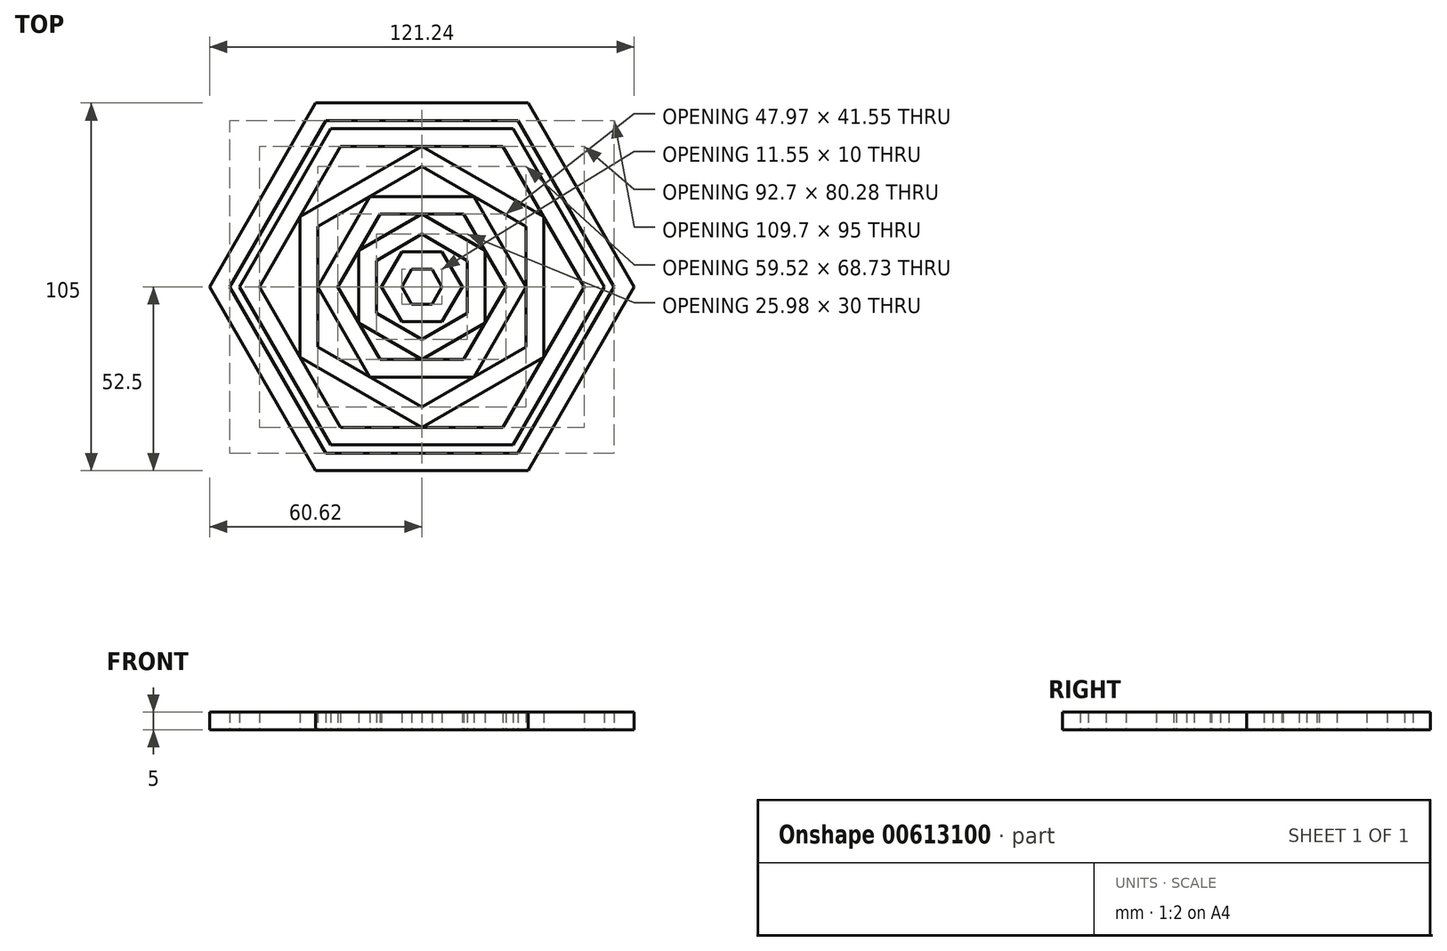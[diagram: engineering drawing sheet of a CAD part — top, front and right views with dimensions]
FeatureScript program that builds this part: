
annotation { "Feature Type Name" : "Feature", "Feature Type Description" : "" }
export const myFeature = defineFeature(function(context is Context, id is Id, definition is map)
    precondition{}
    {
        {
            var Q0;
            Q0=qCreatedBy(makeId("Top.planeOp"),FACE);
            var sketch = newSketch(context, id + "F0", { "sketchPlane" : qUnion([Q0])});
            skCircle(sketch, "E0.cCircle", {"center": v(0, 0) * mm, "radius": 47.5 * mm, "construction": true});
            skLineSegment(sketch, "E0.0", {"start": v(-27.42, 47.5) * mm, "end": v(27.42, 47.5) * mm});
            skLineSegment(sketch, "E0.1", {"start": v(27.42, 47.5) * mm, "end": v(54.85, 0) * mm});
            skLineSegment(sketch, "E0.2", {"start": v(54.85, 0) * mm, "end": v(27.42, -47.5) * mm});
            skLineSegment(sketch, "E0.3", {"start": v(27.42, -47.5) * mm, "end": v(-27.42, -47.5) * mm});
            skLineSegment(sketch, "E0.4", {"start": v(-27.42, -47.5) * mm, "end": v(-54.85, 0) * mm});
            skLineSegment(sketch, "E0.5", {"start": v(-54.85, 0) * mm, "end": v(-27.42, 47.5) * mm});
            skPoint(sketch, "E0.0.midPoint", {"position": v(0, 47.5) * mm});
            skLineSegment(sketch, "E1.0", {"start": v(-60.62, 0) * mm, "end": v(-30.31, 52.5) * mm});
            skLineSegment(sketch, "E1.1", {"start": v(30.31, 52.5) * mm, "end": v(60.62, 0) * mm});
            skLineSegment(sketch, "E1.2", {"start": v(60.62, 0) * mm, "end": v(30.31, -52.5) * mm});
            skLineSegment(sketch, "E1.3", {"start": v(-30.31, 52.5) * mm, "end": v(30.31, 52.5) * mm});
            skLineSegment(sketch, "E1.4", {"start": v(30.31, -52.5) * mm, "end": v(-30.31, -52.5) * mm});
            skLineSegment(sketch, "E1.5", {"start": v(-30.31, -52.5) * mm, "end": v(-60.62, 0) * mm});
            skCircle(sketch, "E2.cCircle", {"center": v(0, 0) * mm, "radius": 5 * mm, "construction": true});
            skLineSegment(sketch, "E2.0", {"start": v(-2.89, 5) * mm, "end": v(2.89, 5) * mm});
            skLineSegment(sketch, "E2.1", {"start": v(2.89, 5) * mm, "end": v(5.77, 0) * mm});
            skLineSegment(sketch, "E2.2", {"start": v(5.77, 0) * mm, "end": v(2.89, -5) * mm});
            skLineSegment(sketch, "E2.3", {"start": v(2.89, -5) * mm, "end": v(-2.89, -5) * mm});
            skLineSegment(sketch, "E2.4", {"start": v(-2.89, -5) * mm, "end": v(-5.77, 0) * mm});
            skLineSegment(sketch, "E2.5", {"start": v(-5.77, 0) * mm, "end": v(-2.89, 5) * mm});
            skPoint(sketch, "E2.0.midPoint", {"position": v(0, 5) * mm});
            skLineSegment(sketch, "E3.0", {"start": v(-11.55, 0) * mm, "end": v(-5.77, 10) * mm});
            skLineSegment(sketch, "E3.1", {"start": v(5.77, 10) * mm, "end": v(11.55, 0) * mm});
            skLineSegment(sketch, "E3.2", {"start": v(11.55, 0) * mm, "end": v(5.77, -10) * mm});
            skLineSegment(sketch, "E3.3", {"start": v(-5.77, 10) * mm, "end": v(5.77, 10) * mm});
            skLineSegment(sketch, "E3.4", {"start": v(5.77, -10) * mm, "end": v(-5.77, -10) * mm});
            skLineSegment(sketch, "E3.5", {"start": v(-5.77, -10) * mm, "end": v(-11.55, 0) * mm});
            skCircle(sketch, "E4.cCircle", {"center": v(0, 0) * mm, "radius": 13 * mm, "construction": true});
            skLineSegment(sketch, "E4.0", {"start": v(13, 7.5) * mm, "end": v(13, -7.5) * mm});
            skLineSegment(sketch, "E4.1", {"start": v(13, -7.5) * mm, "end": v(0, -15) * mm});
            skLineSegment(sketch, "E4.2", {"start": v(0, -15) * mm, "end": v(-13, -7.5) * mm});
            skLineSegment(sketch, "E4.3", {"start": v(-13, -7.5) * mm, "end": v(-13, 7.5) * mm});
            skLineSegment(sketch, "E4.4", {"start": v(-13, 7.5) * mm, "end": v(0, 15) * mm});
            skLineSegment(sketch, "E4.5", {"start": v(0, 15) * mm, "end": v(13, 7.5) * mm});
            skPoint(sketch, "E4.0.midPoint", {"position": v(13, 0) * mm});
            skLineSegment(sketch, "E5.0", {"start": v(-18, 10.39) * mm, "end": v(0, 20.77) * mm});
            skLineSegment(sketch, "E5.1", {"start": v(18, 10.39) * mm, "end": v(18, -10.39) * mm});
            skLineSegment(sketch, "E5.2", {"start": v(18, -10.39) * mm, "end": v(0, -20.77) * mm});
            skLineSegment(sketch, "E5.3", {"start": v(0, 20.77) * mm, "end": v(18, 10.39) * mm});
            skLineSegment(sketch, "E5.4", {"start": v(0, -20.77) * mm, "end": v(-18, -10.39) * mm});
            skLineSegment(sketch, "E5.5", {"start": v(-18, -10.39) * mm, "end": v(-18, 10.39) * mm});
            skCircle(sketch, "E6.cCircle", {"center": v(0, 0) * mm, "radius": 20.77 * mm, "construction": true});
            skLineSegment(sketch, "E6.0", {"start": v(-12, 20.77) * mm, "end": v(12, 20.77) * mm});
            skLineSegment(sketch, "E6.1", {"start": v(12, 20.77) * mm, "end": v(23.99, 0) * mm});
            skLineSegment(sketch, "E6.2", {"start": v(23.99, 0) * mm, "end": v(12, -20.77) * mm});
            skLineSegment(sketch, "E6.3", {"start": v(12, -20.77) * mm, "end": v(-12, -20.77) * mm});
            skLineSegment(sketch, "E6.4", {"start": v(-12, -20.77) * mm, "end": v(-23.99, 0) * mm});
            skLineSegment(sketch, "E6.5", {"start": v(-23.99, 0) * mm, "end": v(-12, 20.77) * mm});
            skPoint(sketch, "E6.0.midPoint", {"position": v(0, 20.77) * mm});
            skLineSegment(sketch, "E7.0", {"start": v(-29.76, 0) * mm, "end": v(-14.88, 25.77) * mm});
            skLineSegment(sketch, "E7.1", {"start": v(14.88, 25.77) * mm, "end": v(29.76, 0) * mm});
            skLineSegment(sketch, "E7.2", {"start": v(29.76, 0) * mm, "end": v(14.88, -25.77) * mm});
            skLineSegment(sketch, "E7.3", {"start": v(-14.88, 25.77) * mm, "end": v(14.88, 25.77) * mm});
            skLineSegment(sketch, "E7.4", {"start": v(14.88, -25.77) * mm, "end": v(-14.88, -25.77) * mm});
            skLineSegment(sketch, "E7.5", {"start": v(-14.88, -25.77) * mm, "end": v(-29.76, 0) * mm});
            skCircle(sketch, "E8.cCircle", {"center": v(0, 0) * mm, "radius": 29.76 * mm, "construction": true});
            skLineSegment(sketch, "E8.0", {"start": v(0, 34.36) * mm, "end": v(29.76, 17.18) * mm});
            skLineSegment(sketch, "E8.1", {"start": v(29.76, 17.18) * mm, "end": v(29.76, -17.18) * mm});
            skLineSegment(sketch, "E8.2", {"start": v(29.76, -17.18) * mm, "end": v(0, -34.36) * mm});
            skLineSegment(sketch, "E8.3", {"start": v(0, -34.36) * mm, "end": v(-29.76, -17.18) * mm});
            skLineSegment(sketch, "E8.4", {"start": v(-29.76, -17.18) * mm, "end": v(-29.76, 17.18) * mm});
            skLineSegment(sketch, "E8.5", {"start": v(-29.76, 17.18) * mm, "end": v(0, 34.36) * mm});
            skPoint(sketch, "E8.0.midPoint", {"position": v(14.88, 25.77) * mm});
            skLineSegment(sketch, "E9.0", {"start": v(-34.76, 20.07) * mm, "end": v(0, 40.14) * mm});
            skLineSegment(sketch, "E9.1", {"start": v(34.76, 20.07) * mm, "end": v(34.76, -20.07) * mm});
            skLineSegment(sketch, "E9.2", {"start": v(34.76, -20.07) * mm, "end": v(0, -40.14) * mm});
            skLineSegment(sketch, "E9.3", {"start": v(0, 40.14) * mm, "end": v(34.76, 20.07) * mm});
            skLineSegment(sketch, "E9.4", {"start": v(0, -40.14) * mm, "end": v(-34.76, -20.07) * mm});
            skLineSegment(sketch, "E9.5", {"start": v(-34.76, -20.07) * mm, "end": v(-34.76, 20.07) * mm});
            skPoint(sketch, "E10.center", {"position": v(0, 24.3) * mm});
            skCircle(sketch, "E11.cCircle", {"center": v(0, 0) * mm, "radius": 40.14 * mm, "construction": true});
            skLineSegment(sketch, "E11.0", {"start": v(46.35, 0) * mm, "end": v(23.17, -40.14) * mm});
            skLineSegment(sketch, "E11.1", {"start": v(23.17, -40.14) * mm, "end": v(-23.17, -40.14) * mm});
            skLineSegment(sketch, "E11.2", {"start": v(-23.17, -40.14) * mm, "end": v(-46.35, 0) * mm});
            skLineSegment(sketch, "E11.3", {"start": v(-46.35, 0) * mm, "end": v(-23.17, 40.14) * mm});
            skLineSegment(sketch, "E11.4", {"start": v(-23.17, 40.14) * mm, "end": v(23.17, 40.14) * mm});
            skLineSegment(sketch, "E11.5", {"start": v(23.17, 40.14) * mm, "end": v(46.35, 0) * mm});
            skPoint(sketch, "E11.0.midPoint", {"position": v(34.76, -20.07) * mm});
            skLineSegment(sketch, "E12.0", {"start": v(26.06, 45.14) * mm, "end": v(52.12, 0) * mm});
            skLineSegment(sketch, "E12.1", {"start": v(26.06, -45.14) * mm, "end": v(-26.06, -45.14) * mm});
            skLineSegment(sketch, "E12.2", {"start": v(-26.06, -45.14) * mm, "end": v(-52.12, 0) * mm});
            skLineSegment(sketch, "E12.3", {"start": v(52.12, 0) * mm, "end": v(26.06, -45.14) * mm});
            skLineSegment(sketch, "E12.4", {"start": v(-52.12, 0) * mm, "end": v(-26.06, 45.14) * mm});
            skLineSegment(sketch, "E12.5", {"start": v(-26.06, 45.14) * mm, "end": v(26.06, 45.14) * mm});
            skSolve(sketch);
        }
        {
            var Q0;
            Q0=makeQuery(id+"F0.imprint","IMPRINT",FACE,{"disambiguationData":[TD([[makeQuery(id+"F0.imprint","IMPRINT",EDGE,{"derivedFrom":sQuery(id+"F0.wireOp",EDGE,"E9.0")}),-1.0]])]});
            var Q1;
            Q1=makeQuery(id+"F0.imprint","IMPRINT",FACE,{"disambiguationData":[TD([[makeQuery(id+"F0.imprint","IMPRINT",EDGE,{"derivedFrom":sQuery(id+"F0.wireOp",EDGE,"E7.0")}),-1.0]])]});
            var Q2;
            Q2=makeQuery(id+"F0.imprint","IMPRINT",FACE,{"disambiguationData":[TD([[makeQuery(id+"F0.imprint","IMPRINT",EDGE,{"derivedFrom":sQuery(id+"F0.wireOp",EDGE,"E4.0")}),1.0]])]});
            var Q3;
            Q3=makeQuery(id+"F0.imprint","IMPRINT",FACE,{"disambiguationData":[TD([[makeQuery(id+"F0.imprint","IMPRINT",EDGE,{"derivedFrom":sQuery(id+"F0.wireOp",EDGE,"E2.0")}),1.0]])]});
            var Q4;
            Q4=makeQuery(id+"F0.imprint","IMPRINT",FACE,{"disambiguationData":[TD([[makeQuery(id+"F0.imprint","IMPRINT",EDGE,{"derivedFrom":sQuery(id+"F0.wireOp",EDGE,"E12.0")}),-1.0]])]});
            var Q5;
            Q5=makeQuery(id+"F0.imprint","IMPRINT",FACE,{"disambiguationData":[TD([[makeQuery(id+"F0.imprint","IMPRINT",EDGE,{"derivedFrom":sQuery(id+"F0.wireOp",EDGE,"E0.0")}),1.0]])]});
            extrude(context, id + "F1", {"entities" : qUnion([Q0, Q1, Q2, Q3, Q4, Q5]), "depth" : 5 * mm, "offsetDistance" : 25 * mm});
        }
    });
